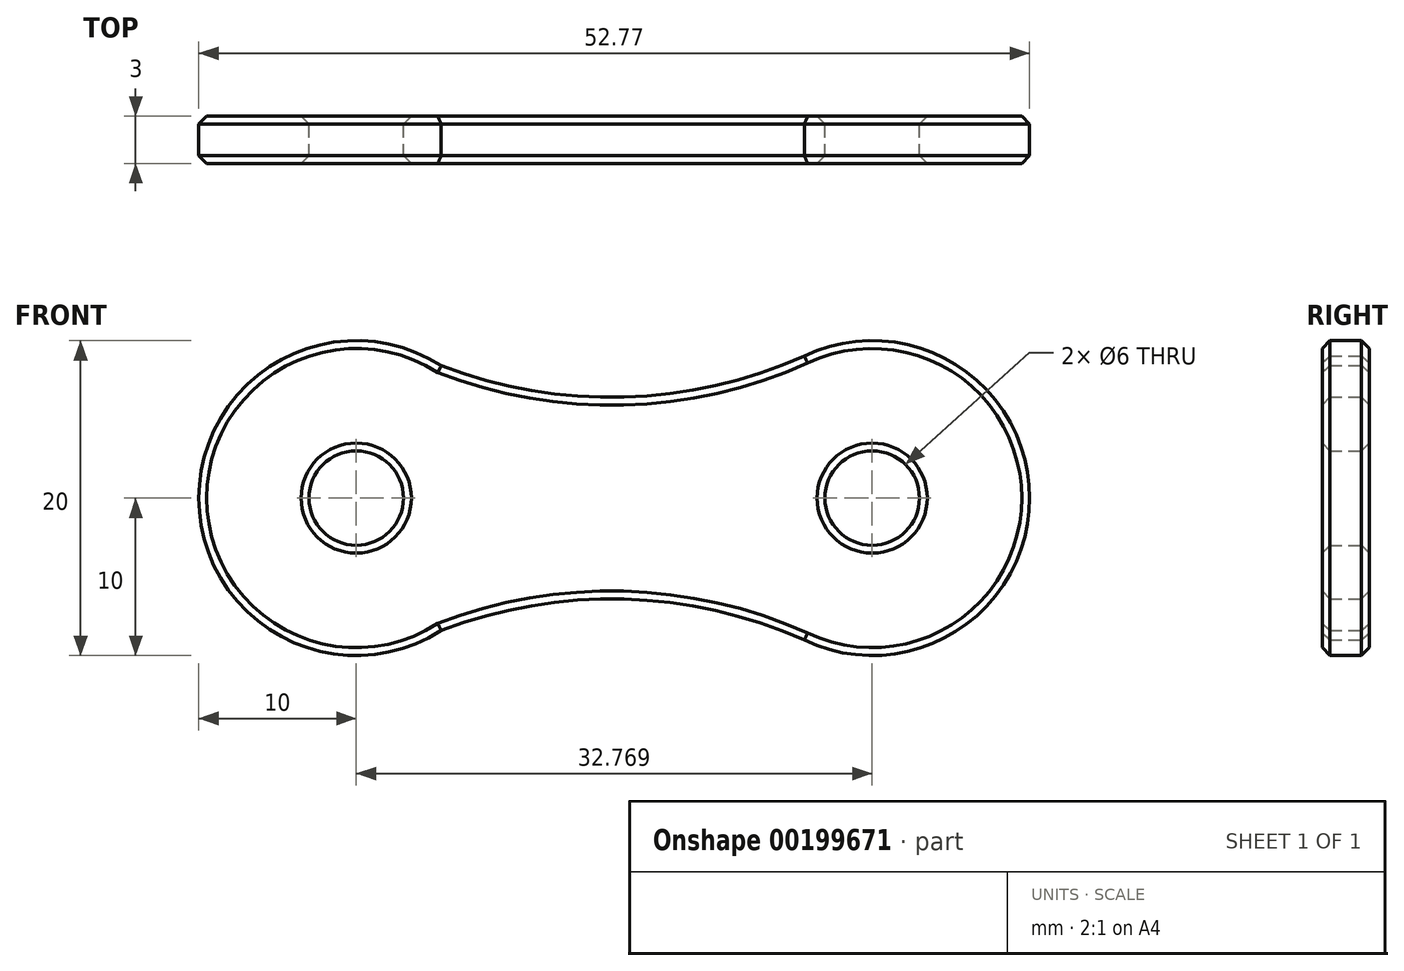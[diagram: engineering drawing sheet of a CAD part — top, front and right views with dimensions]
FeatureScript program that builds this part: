
annotation { "Feature Type Name" : "Feature", "Feature Type Description" : "" }
export const myFeature = defineFeature(function(context is Context, id is Id, definition is map)
    precondition{}
    {
        {
            var Q0;
            Q0=qCreatedBy(makeId("Front.planeOp"),FACE);
            var sketch = newSketch(context, id + "F0", { "sketchPlane" : qUnion([Q0])});
            skArc(sketch, "E0", {"start": v(11.79, -9.02) * mm, "mid": v(26.1, 0) * mm, "end": v(11.79, 9.02) * mm});
            skArc(sketch, "E1", {"start": v(-11.27, 8.42) * mm, "mid": v(-26.67, 0) * mm, "end": v(-11.27, -8.42) * mm});
            skArc(sketch, "E2", {"start": v(11.79, -9.02) * mm, "mid": v(0.32, -6.42) * mm, "end": v(-11.27, -8.42) * mm});
            skArc(sketch, "E3", {"start": v(-11.27, 8.42) * mm, "mid": v(0.32, 6.42) * mm, "end": v(11.79, 9.02) * mm});
            skCircle(sketch, "E4", {"center": v(-16.67, 0) * mm, "radius": 3 * mm});
            skCircle(sketch, "E5", {"center": v(16.1, 0) * mm, "radius": 3 * mm});
            skSolve(sketch);
        }
        {
            var Q0;
            Q0=makeQuery(id+"F0.imprint","IMPRINT",FACE,{"disambiguationData":[TD([[makeQuery(id+"F0.imprint","IMPRINT",EDGE,{"derivedFrom":sQuery(id+"F0.wireOp",EDGE,"E0")}),1.0]])]});
            extrude(context, id + "F1", {"entities" : qUnion([Q0]), "depth" : 3 * mm});
        }
        {
            var Q0;
            Q0=makeQuery(id+"F1.opExtrude","CAP_FACE",FACE,{"disambiguationData":[OSD([sQuery(id+"F0.wireOp",EDGE,"E0"),sQuery(id+"F0.wireOp",EDGE,"E1"),sQuery(id+"F0.wireOp",EDGE,"E2"),sQuery(id+"F0.wireOp",EDGE,"E3"),sQuery(id+"F0.wireOp",EDGE,"E4"),sQuery(id+"F0.wireOp",EDGE,"E5")])],"isStart":false});
            var Q1;
            Q1=makeQuery(id+"F1.opExtrude","CAP_FACE",FACE,{"disambiguationData":[OSD([sQuery(id+"F0.wireOp",EDGE,"E0"),sQuery(id+"F0.wireOp",EDGE,"E1"),sQuery(id+"F0.wireOp",EDGE,"E2"),sQuery(id+"F0.wireOp",EDGE,"E3"),sQuery(id+"F0.wireOp",EDGE,"E4"),sQuery(id+"F0.wireOp",EDGE,"E5")])],"isStart":true});
            chamfer(context, id + "F2", {"entities" : qUnion([Q0, Q1]), "width" : .5 * mm, "tangentPropagation" : true});
        }
    });
